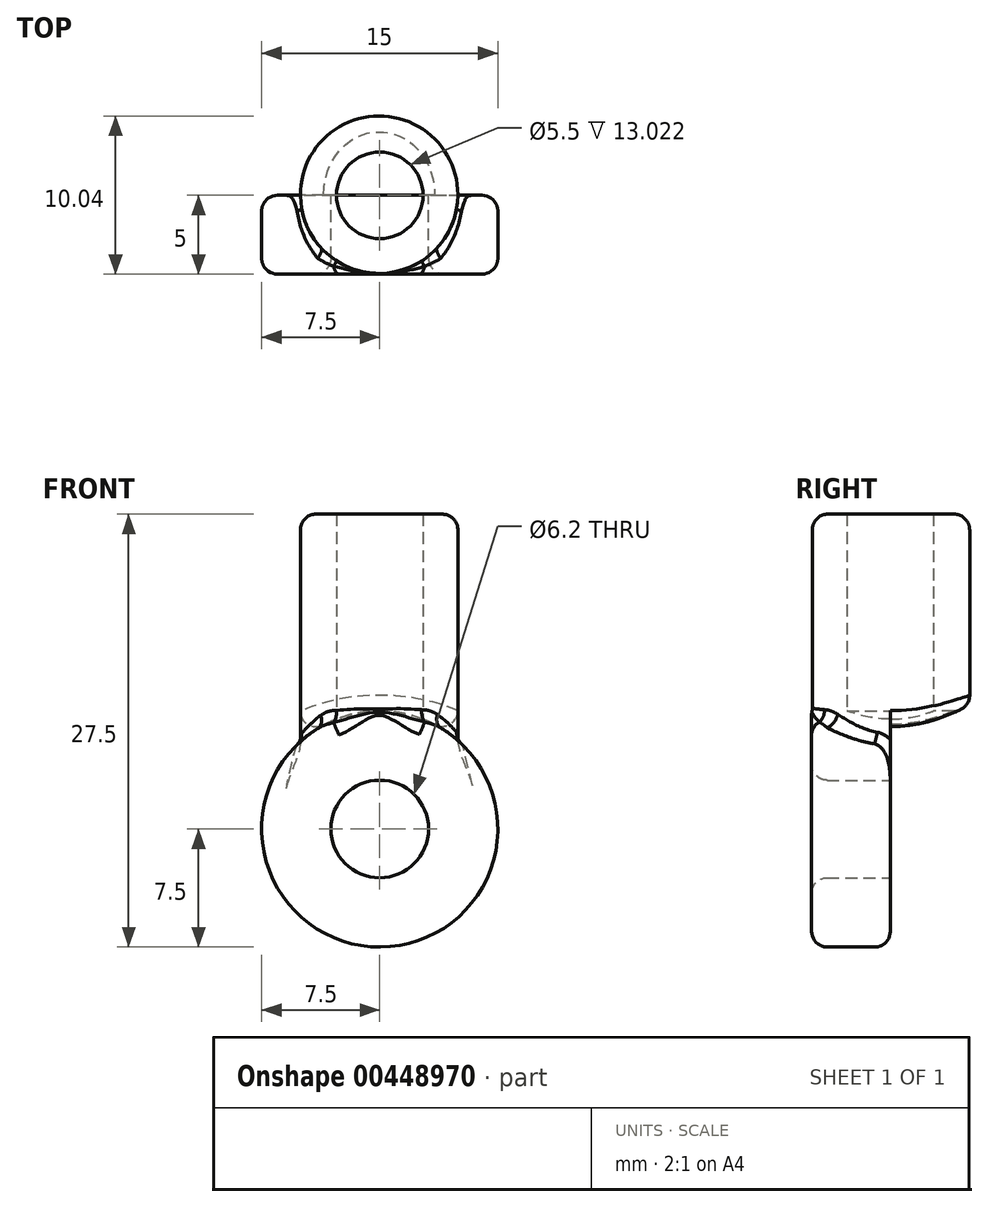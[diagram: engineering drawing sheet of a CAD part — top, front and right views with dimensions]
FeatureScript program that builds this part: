
annotation { "Feature Type Name" : "Feature", "Feature Type Description" : "" }
export const myFeature = defineFeature(function(context is Context, id is Id, definition is map)
    precondition{}
    {
        {
            var Q0;
            Q0=qCreatedBy(makeId("Top.planeOp"),FACE);
            var sketch = newSketch(context, id + "F0", { "sketchPlane" : qUnion([Q0])});
            skCircle(sketch, "E0", {"center": v(-0.04, 0.04) * mm, "radius": 5 * mm});
            skCircle(sketch, "E1", {"center": v(0, 0) * mm, "radius": 2.75 * mm});
            skSolve(sketch);
        }
        {
            var Q0;
            Q0=makeQuery(id+"F0.imprint","IMPRINT",FACE,{"disambiguationData":[TD([[makeQuery(id+"F0.imprint","IMPRINT",EDGE,{"derivedFrom":sQuery(id+"F0.wireOp",EDGE,"E0")}),1.0]])]});
            extrude(context, id + "F1", {"entities" : qUnion([Q0]), "depth" : 20 * mm});
        }
        {
            var Q0;
            Q0=qCreatedBy(makeId("Front.planeOp"),FACE);
            var sketch = newSketch(context, id + "F2", { "sketchPlane" : qUnion([Q0])});
            skCircle(sketch, "E2", {"center": v(0, 0) * mm, "radius": 7.5 * mm});
            skCircle(sketch, "E3", {"center": v(0, 0) * mm, "radius": 3.1 * mm});
            skSolve(sketch);
        }
        {
            var Q0;
            Q0 = qSketchRegion(id + "F2", true);
            extrude(context, id + "F3", {"entities" : qUnion([Q0]), "operationType" : NewBodyOperationType.ADD, "depth" : 5 * mm});
        }
        {
            var Q0;
            Q0 = qSketchRegion(id + "F2", true);
            var Q1;
            {var subQ1=sQuery(id+"F0.wireOp",EDGE,"E0");var subQ2=sQuery(id+"F2.wireOp",EDGE,"E2");Q1=makeQuery(id+"F3.boolean.opBoolean","SPLIT",FACE,{"disambiguationData":[TD([makeQuery(id+"F3.opExtrude","SWEPT_FACE",FACE,{"disambiguationData":[OSD([subQ2])]})])],"derivedFrom":makeQuery(id+"F1.opExtrude","SWEPT_FACE",FACE,{"disambiguationData":[OSD([subQ1])]})});}
            extrude(context, id + "F4", {"entities" : qUnion([Q0]), "operationType" : NewBodyOperationType.REMOVE, "endBound" : BoundingType.THROUGH_ALL, "oppositeDirection" : true, "endBoundEntityFace" : qUnion([Q1]), "depth" : 25 * mm});
        }
        {
            var Q0;
            Q0=makeQuery(id+"F2.imprint","IMPRINT",FACE,{"disambiguationData":[TD([[makeQuery(id+"F2.imprint","IMPRINT",EDGE,{"derivedFrom":sQuery(id+"F2.wireOp",EDGE,"E3")}),1.0]])]});
            extrude(context, id + "F5", {"entities" : qUnion([Q0]), "operationType" : NewBodyOperationType.REMOVE, "oppositeDirection" : true, "depth" : 25 * mm, "hasSecondDirection" : true, "secondDirectionOppositeDirection" : false, "secondDirectionDepth" : 25 * mm});
        }
        {
            var Q0;
            Q0=makeQuery(id+"F3.opExtrude","CAP_EDGE",EDGE,{"disambiguationData":[OSD([sQuery(id+"F2.wireOp",EDGE,"E2")])],"isStart":false});
            var Q1;
            Q1=makeQuery(id+"F3.opExtrude","CAP_FACE",FACE,{"disambiguationData":[OSD([sQuery(id+"F2.wireOp",EDGE,"E2"),sQuery(id+"F2.wireOp",EDGE,"E3")])],"isStart":false});
            var Q2;
            {var subQ0=sQuery(id+"F2.wireOp",EDGE,"E2");Q2=makeQuery(id+"F3.boolean.opBoolean","SPLIT",EDGE,{"disambiguationData":[TD([makeQuery(id+"F1.opExtrude","SWEPT_FACE",FACE,{"disambiguationData":[OSD([sQuery(id+"F0.wireOp",EDGE,"E0")])]})])],"derivedFrom":makeQuery(id+"F3.opExtrude","CAP_EDGE",EDGE,{"disambiguationData":[OSD([subQ0])],"isStart":true})});}
            fillet(context, id + "F6", {"entities" : qUnion([Q0, Q1, Q2]), "radius" : 1 * mm, "tangentPropagation" : true, "allowEdgeOverflow" : false});
        }
        {
            var Q0;
            Q0=makeQuery(id+"F3.boolean.opBoolean","INTERSECT",EDGE,{"derivedFrom":[makeQuery(id+"F1.opExtrude","SWEPT_FACE",FACE,{"disambiguationData":[OSD([sQuery(id+"F0.wireOp",EDGE,"E0")])]}),makeQuery(id+"F3.opExtrude","SWEPT_FACE",FACE,{"disambiguationData":[OSD([sQuery(id+"F2.wireOp",EDGE,"E2")])]})]});
            var Q1;
            {var subQ0=sQuery(id+"F2.wireOp",EDGE,"E2");var subQ4=sQuery(id+"F0.wireOp",EDGE,"E0");var subQ6=makeQuery(id+"F3.opExtrude","SWEPT_FACE",FACE,{"disambiguationData":[OSD([subQ0])]});Q1=makeQuery(id+"F6.opFillet","BLEND_EDGE",EDGE,{"blendedFrom":[makeQuery(id+"F3.opExtrude","CAP_EDGE",EDGE,{"disambiguationData":[OSD([subQ0])],"isStart":false}),makeQuery(id+"F4.boolean.opBoolean","SPLIT",FACE,{"disambiguationData":[TD([subQ6])],"derivedFrom":makeQuery(id+"F3.boolean.opBoolean","SPLIT",FACE,{"disambiguationData":[TD([subQ6])],"derivedFrom":makeQuery(id+"F1.opExtrude","SWEPT_FACE",FACE,{"disambiguationData":[OSD([subQ4])]})})})],"blendedInto":[makeQuery(id+"F4.boolean.opBoolean","SPLIT",FACE,{"disambiguationData":[TD([subQ6])],"derivedFrom":makeQuery(id+"F3.boolean.opBoolean","SPLIT",FACE,{"disambiguationData":[TD([subQ6])],"derivedFrom":makeQuery(id+"F1.opExtrude","SWEPT_FACE",FACE,{"disambiguationData":[OSD([subQ4])]})})})]});}
            fillet(context, id + "F7", {"entities" : qUnion([Q0, Q1]), "radius" : 1 * mm, "tangentPropagation" : true, "allowEdgeOverflow" : false});
        }
        {
            var Q0;
            {var subQ0=sQuery(id+"F2.wireOp",EDGE,"E2");var subQ2=sQuery(id+"F0.wireOp",EDGE,"E0");Q0=makeQuery(id+"F4.boolean.opBoolean","INTERSECT",EDGE,{"derivedFrom":[makeQuery(id+"F3.boolean.opBoolean","SPLIT",FACE,{"disambiguationData":[TD([makeQuery(id+"F3.opExtrude","SWEPT_FACE",FACE,{"disambiguationData":[OSD([subQ0])]})])],"derivedFrom":makeQuery(id+"F1.opExtrude","SWEPT_FACE",FACE,{"disambiguationData":[OSD([subQ2])]})}),makeQuery(id+"F4.opExtrude","SWEPT_FACE",FACE,{"disambiguationData":[OSD([subQ0])]})]});}
            var Q1;
            Q1=makeQuery(id+"F1.opExtrude","CAP_EDGE",EDGE,{"disambiguationData":[OSD([sQuery(id+"F0.wireOp",EDGE,"E0")])],"isStart":false});
            fillet(context, id + "F8", {"entities" : qUnion([Q0, Q1]), "radius" : 1 * mm, "tangentPropagation" : true, "allowEdgeOverflow" : false});
        }
    });
